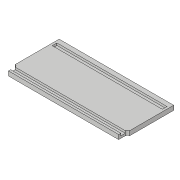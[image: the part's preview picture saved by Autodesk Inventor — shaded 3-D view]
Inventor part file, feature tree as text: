
AUTODESK INVENTOR PART (.ipt)
format: ipt  version: 2018.3 (Build 223284000, 284)  size: 132,608 bytes
history: native  units: in
note: dims shown in document units (in); Inventor stores cm internally (conversion verified against a paired STEP export)
features: extrude x4, sketch x4, fillet x2
ambient origin geometry x8: Origin, YZ Plane, XZ Plane, XY Plane, X Axis, Y Axis, Z Axis, Center Point
bodies: Solid1 (feature_tree)
feature tree (10):
  extrude  "Extrusion1"  Depth=1.5in
  extrude  "Extrusion2"  Depth=0.126in
  extrude  "Extrusion3"  Depth=0.0625in TaperAngle=0.0deg
  extrude  "Extrusion4"  Depth=0.135in
  fillet  "Fillet1"  Radius=0.0625in
  fillet  "Fillet2"  Radius=0.0625in
  sketch  "Sketch1"  dims[d0=3.25in d1=1.5in]
  sketch  "Sketch2"  dims[d2=0.125in d3=0.0in d6=0.126in]
  sketch  "Sketch3"  dims[d7=0.0625in d8=0.0625in d9=0.0in]
  sketch  "Sketch4"  dims[d10=0.125in d11=0.135in d12=0.0625in d13=0.0625in d14=0.0625in d15=0.0625in d16=0.125in d17=0.135in d18=0.0625in d19=0.0in d20=0.0625in d21=0.25in d22=0.25in d23=0.0625in d24=1.0in d25=0.0in d26=0.0625in d27=0.0625in]
